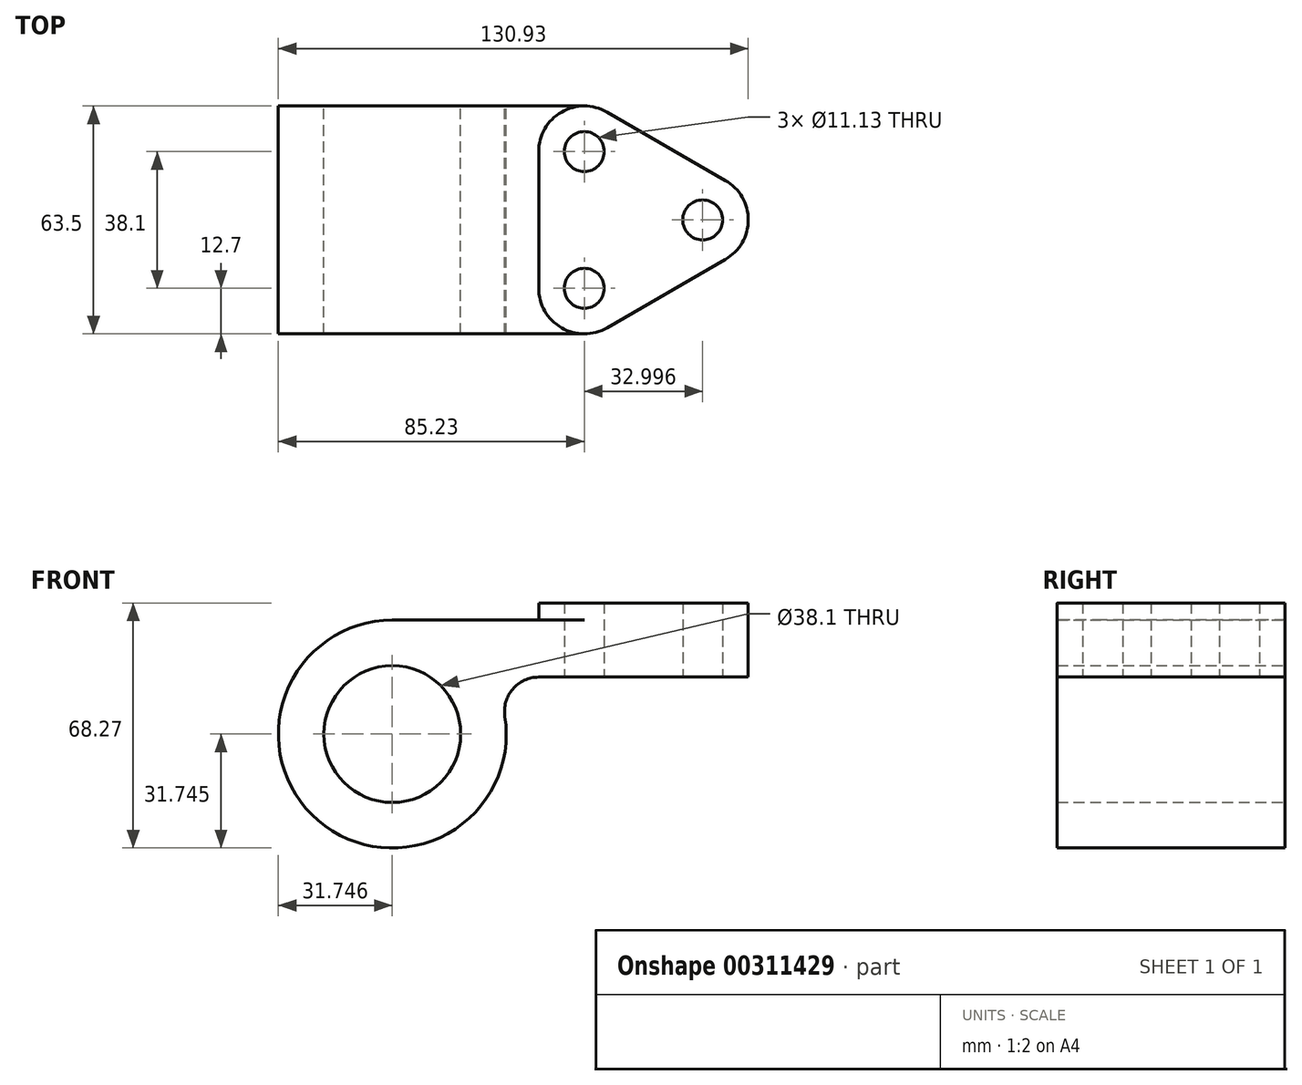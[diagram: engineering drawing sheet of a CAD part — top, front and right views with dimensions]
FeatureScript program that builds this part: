
annotation { "Feature Type Name" : "Feature", "Feature Type Description" : "" }
export const myFeature = defineFeature(function(context is Context, id is Id, definition is map)
    precondition{}
    {
        {
            var Q0;
            Q0=qCreatedBy(makeId("Top.planeOp"),FACE);
            var sketch = newSketch(context, id + "F0", { "sketchPlane" : qUnion([Q0])});
            skLineSegment(sketch, "E0", {"start": v(0, 19.05) * mm, "end": v(0, -19.05) * mm});
            skArc(sketch, "E1", {"start": v(19.05, 30.05) * mm, "mid": v(6.35, 30.05) * mm, "end": v(0, 19.05) * mm});
            skArc(sketch, "E2", {"start": v(0, -19.05) * mm, "mid": v(6.35, -30.05) * mm, "end": v(19.05, -30.05) * mm});
            skLineSegment(sketch, "E3", {"start": v(19.05, 30.05) * mm, "end": v(52.05, 11) * mm});
            skLineSegment(sketch, "E4", {"start": v(19.05, -30.05) * mm, "end": v(52.05, -11) * mm});
            skArc(sketch, "E5", {"start": v(52.05, -11) * mm, "mid": v(58.4, 0) * mm, "end": v(52.05, 11) * mm});
            skCircle(sketch, "E6", {"center": v(12.7, 19.05) * mm, "radius": 5.56 * mm});
            skCircle(sketch, "E7", {"center": v(45.7, 0) * mm, "radius": 5.56 * mm});
            skCircle(sketch, "E8", {"center": v(12.7, -19.05) * mm, "radius": 5.56 * mm});
            skSolve(sketch);
        }
        {
            var Q0;
            Q0 = qSketchRegion(id + "F0", true);
            extrude(context, id + "F1", {"entities" : qUnion([Q0]), "depth" : 20.65 * mm});
        }
        {
            var Q0;
            Q0=qCreatedBy(makeId("Front.planeOp"),FACE);
            var sketch = newSketch(context, id + "F2", { "sketchPlane" : qUnion([Q0])});
            skCircle(sketch, "E9", {"center": v(-40.78, -15.88) * mm, "radius": 19.05 * mm});
            skArc(sketch, "E10", {"start": v(-40.78, 15.88) * mm, "mid": v(-61.44, -40) * mm, "end": v(-9.41, -11) * mm});
            skLineSegment(sketch, "E11", {"start": v(-40.78, 15.88) * mm, "end": v(12.7, 15.88) * mm});
            skArc(sketch, "E12", {"start": v(0, 0) * mm, "mid": v(-7.23, -3.33) * mm, "end": v(-9.41, -11) * mm});
            skLineSegment(sketch, "E13", {"start": v(12.7, 15.88) * mm, "end": v(12.7, 0) * mm});
            skLineSegment(sketch, "E14", {"start": v(0, 0) * mm, "end": v(12.7, 0) * mm});
            skSolve(sketch);
        }
        {
            var Q0;
            Q0 = qSketchRegion(id + "F2", true);
            extrude(context, id + "F3", {"entities" : qUnion([Q0]), "operationType" : NewBodyOperationType.ADD, "endBound" : BoundingType.SYMMETRIC, "depth" : 63.5 * mm});
        }
        {
            var Q0;
            Q0=makeQuery(id+"F1.opExtrude","CAP_FACE",FACE,{"disambiguationData":[OSD([sQuery(id+"F0.wireOp",EDGE,"E0"),sQuery(id+"F0.wireOp",EDGE,"E1"),sQuery(id+"F0.wireOp",EDGE,"E2"),sQuery(id+"F0.wireOp",EDGE,"E3"),sQuery(id+"F0.wireOp",EDGE,"E4"),sQuery(id+"F0.wireOp",EDGE,"E5"),sQuery(id+"F0.wireOp",EDGE,"E6"),sQuery(id+"F0.wireOp",EDGE,"E7"),sQuery(id+"F0.wireOp",EDGE,"E8")])],"isStart":false});
            var sketch = newSketch(context, id + "F4", { "sketchPlane" : qUnion([Q0])});
            skArc(sketch, "E15", {"start": v(12.7, 24.61) * mm, "mid": v(7.14, 19.05) * mm, "end": v(12.7, 13.49) * mm});
            skLineSegment(sketch, "E16", {"start": v(12.7, 13.49) * mm, "end": v(12.7, 24.61) * mm});
            skLineSegment(sketch, "E17", {"start": v(12.7, -24.61) * mm, "end": v(12.7, -13.49) * mm});
            skArc(sketch, "E18", {"start": v(12.7, -13.49) * mm, "mid": v(7.14, -19.05) * mm, "end": v(12.7, -24.61) * mm});
            skSolve(sketch);
        }
        {
            var Q0;
            Q0 = qSketchRegion(id + "F4", true);
            extrude(context, id + "F5", {"entities" : qUnion([Q0]), "operationType" : NewBodyOperationType.REMOVE, "endBound" : BoundingType.THROUGH_ALL, "oppositeDirection" : true, "depth" : 25.4 * mm});
        }
    });
